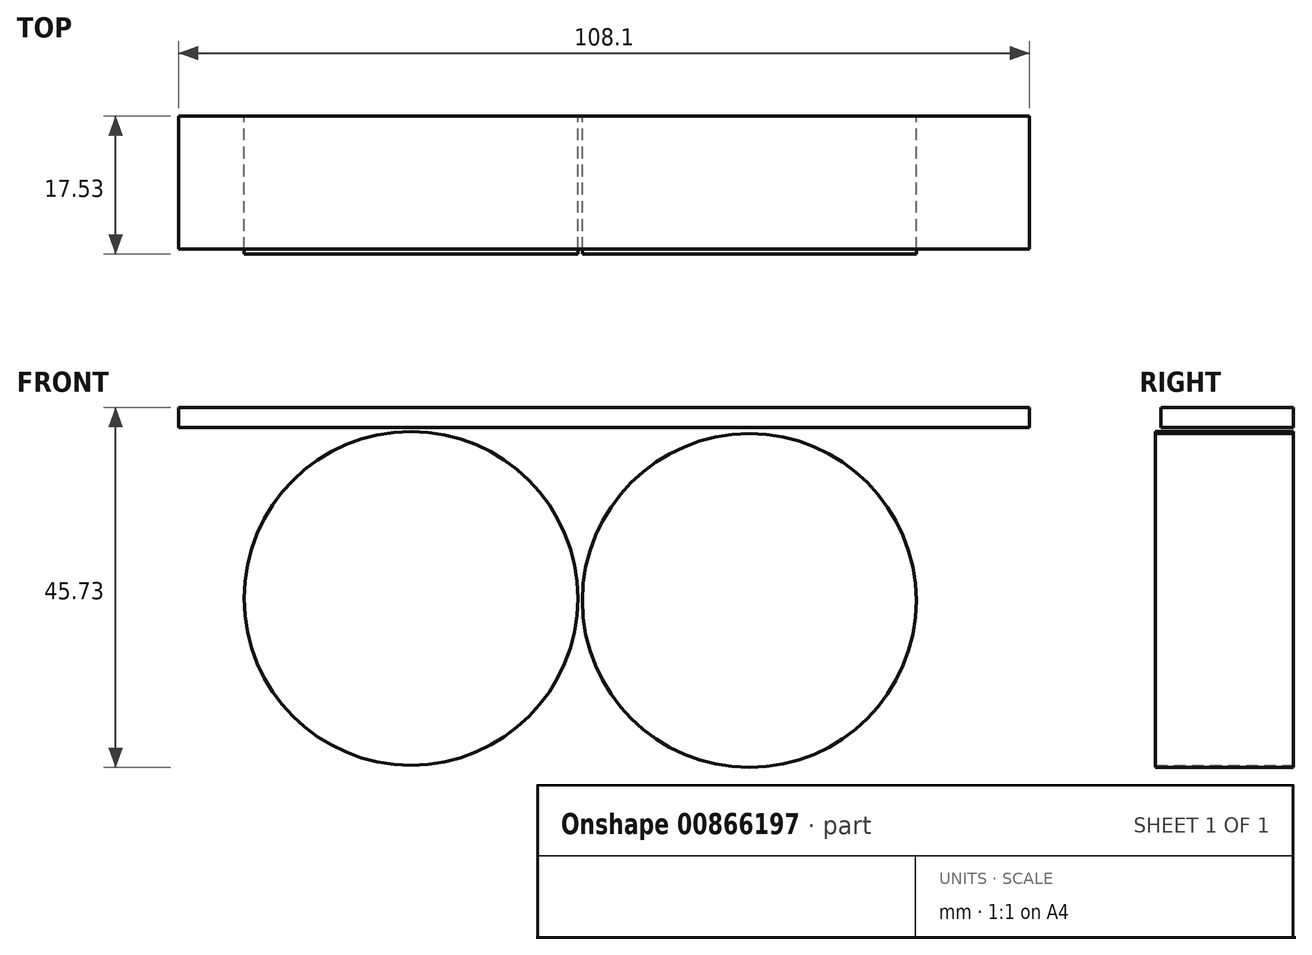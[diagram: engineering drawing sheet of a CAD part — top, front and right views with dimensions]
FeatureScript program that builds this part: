
annotation { "Feature Type Name" : "Feature", "Feature Type Description" : "" }
export const myFeature = defineFeature(function(context is Context, id is Id, definition is map)
    precondition{}
    {
        {
            var Q0;
            Q0=qCreatedBy(makeId("Top.planeOp"),FACE);
            var sketch = newSketch(context, id + "F0", { "sketchPlane" : qUnion([Q0])});
            skLineSegment(sketch, "E0.bottom", {"start": v(-72.5, 0) * mm, "end": v(35.6, 0) * mm});
            skLineSegment(sketch, "E0.top", {"start": v(-72.5, -16.88) * mm, "end": v(35.6, -16.88) * mm});
            skLineSegment(sketch, "E0.left", {"start": v(-72.5, 0) * mm, "end": v(-72.5, -16.88) * mm});
            skLineSegment(sketch, "E0.right", {"start": v(35.6, 0) * mm, "end": v(35.6, -16.88) * mm});
            skSolve(sketch);
        }
        {
            var Q0;
            Q0 = qSketchRegion(id + "F0", true);
            extrude(context, id + "F1", {"entities" : qUnion([Q0]), "depth" : 2.54 * mm, "offsetDistance" : 25.4 * mm});
        }
        {
            var Q0;
            Q0=qCreatedBy(makeId("Front.planeOp"),FACE);
            var sketch = newSketch(context, id + "F2", { "sketchPlane" : qUnion([Q0])});
            skCircle(sketch, "E1", {"center": v(-42.98, -21.7) * mm, "radius": 21.2 * mm});
            skCircle(sketch, "E2", {"center": v(0, -21.99) * mm, "radius": 21.2 * mm});
            skSolve(sketch);
        }
        {
            var Q0;
            Q0 = qSketchRegion(id + "F2", true);
            extrude(context, id + "F3", {"entities" : qUnion([Q0]), "depth" : 17.53 * mm, "offsetDistance" : 25.4 * mm});
        }
    });
